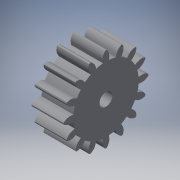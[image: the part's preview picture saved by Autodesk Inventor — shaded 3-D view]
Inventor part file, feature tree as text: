
AUTODESK INVENTOR PART (.ipt)
format: ipt  version: 2018 (Build 220112000, 112)  size: 346,624 bytes
history: native  units: in
note: dims shown in document units (in); Inventor stores cm internally (conversion verified against a paired STEP export)
features: extrude x1, sketch x1
ambient origin geometry x8: Origin, YZ Plane, XZ Plane, XY Plane, X Axis, Y Axis, Z Axis, Center Point
bodies: Solid1 (feature_tree)
feature tree (2):
  extrude  "Extrusion1"  Depth=0.4882in TaperAngle=360.0deg
  sketch  "Sketch1"  dims[d1=1.0in d2=6.2992in d4=360.0deg d6=0.1969in d7=0.4882in d8=0.0in]
